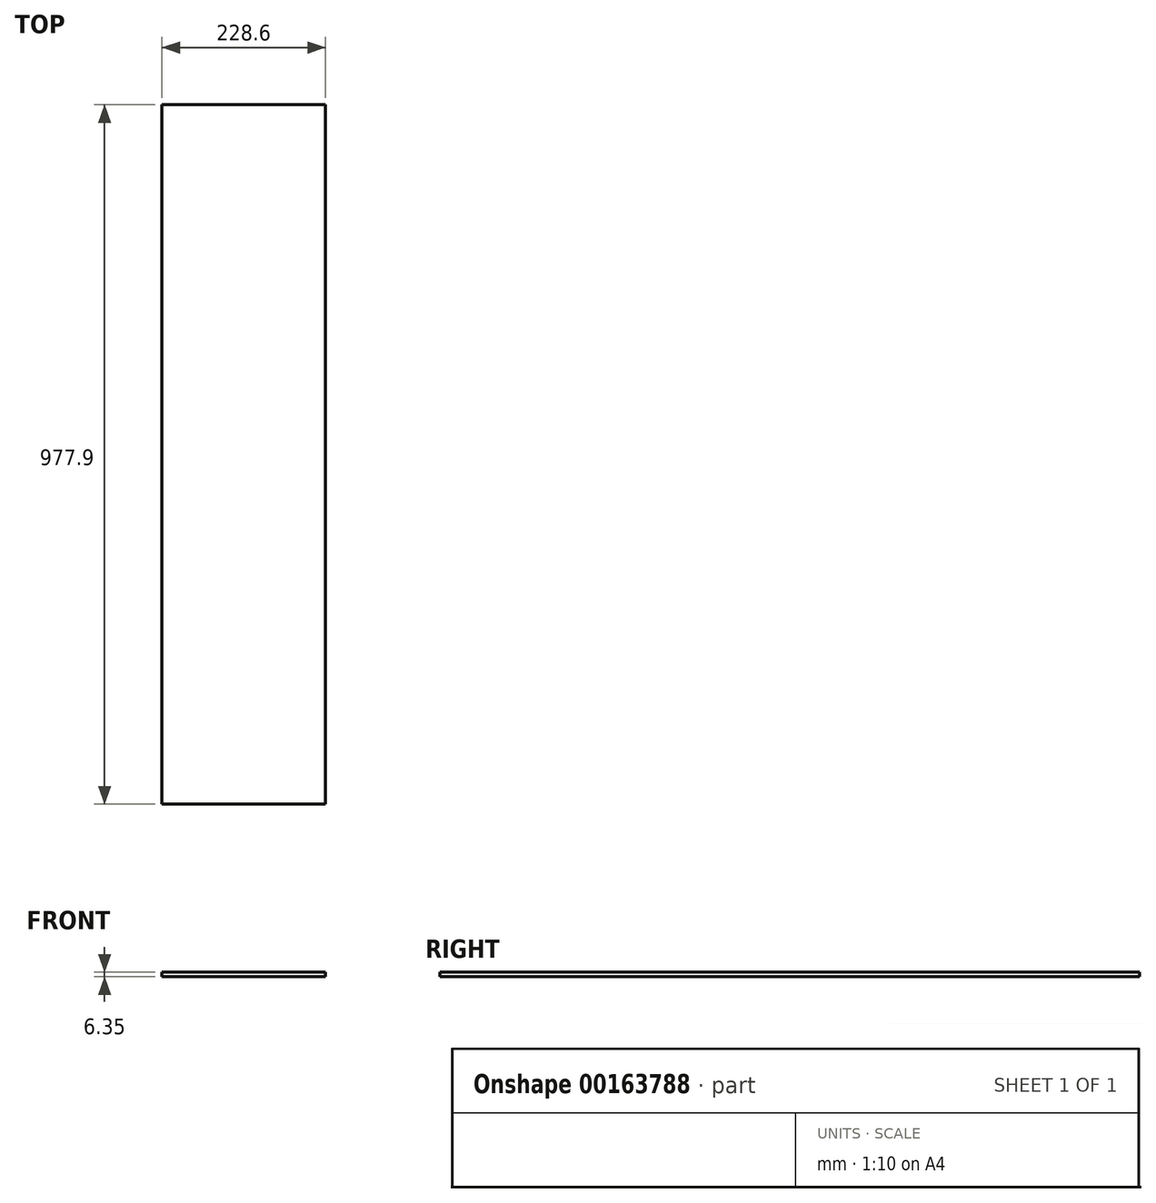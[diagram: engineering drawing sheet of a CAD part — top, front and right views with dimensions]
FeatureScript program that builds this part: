
annotation { "Feature Type Name" : "Feature", "Feature Type Description" : "" }
export const myFeature = defineFeature(function(context is Context, id is Id, definition is map)
    precondition{}
    {
        {
            var Q0;
            Q0=qCreatedBy(makeId("Top.planeOp"),FACE);
            var sketch = newSketch(context, id + "F0", { "sketchPlane" : qUnion([Q0])});
            skLineSegment(sketch, "E0.bottom", {"start": v(114.3, 488.95) * mm, "end": v(-114.3, 488.95) * mm});
            skLineSegment(sketch, "E0.top", {"start": v(114.3, -488.95) * mm, "end": v(-114.3, -488.95) * mm});
            skLineSegment(sketch, "E0.left", {"start": v(114.3, 488.95) * mm, "end": v(114.3, -488.95) * mm});
            skLineSegment(sketch, "E0.right", {"start": v(-114.3, 488.95) * mm, "end": v(-114.3, -488.95) * mm});
            skPoint(sketch, "E0.middle", {"position": v(0, 0) * mm});
            skSolve(sketch);
        }
        {
            var Q0;
            Q0=qSketchRegion(id+"F0",true);
            extrude(context, id + "F1", {"entities" : qUnion([Q0]), "depth" : 6.35 * mm});
        }
    });
